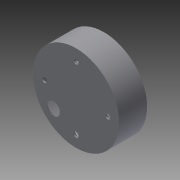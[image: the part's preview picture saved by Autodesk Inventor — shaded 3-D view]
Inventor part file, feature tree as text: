
AUTODESK INVENTOR PART (.ipt)
format: ipt  version: 2014 (Build 180170000, 170)  size: 233,472 bytes
history: native  units: mm
features: sketch x9, extrude x8, chamfer x5, projected_geometry x3, plane x1
ambient origin geometry x8: Origin, YZ Plane, XZ Plane, XY Plane, X Axis, Y Axis, Z Axis, Center Point
bodies: Solid1 (feature_tree)
feature tree (26):
  extrude  "Extrusion1"  Depth=3.0mm TaperAngle=0.0deg
  extrude  "Extrusion2"  Depth=19.0mm TaperAngle=0.0deg
  extrude  "Extrusion3"  Depth=4.0mm
  chamfer  "Chamfer1"  Distance=14.0mm
  extrude  "Extrusion4"  Depth=6.0mm TaperAngle=45.0deg
  chamfer  "Chamfer2"  Distance=10.0mm
  sketch  "Sketch5"  dims[d9=4.0mm]
  extrude  "Extrusion5"  Depth=6.0mm TaperAngle=0.0deg
  extrude  "Extrusion6"  Depth=6.0mm TaperAngle=45.0deg
  chamfer  "Chamfer3"  Distance=25.0mm
  plane  "Work Plane1"
  extrude  "Extrusion9"  Depth=6.0mm
  chamfer  "Chamfer5"  Distance=2.5mm
  extrude  "Extrusion10"  Depth=6.0mm
  chamfer  "Chamfer6"  Distance=6.0mm
  sketch  "Sketch1"  dims[d0=68.0mm d1=3.0mm d2=0.0mm]
  sketch  "Sketch2"  dims[d3=62.0mm d4=19.0mm d5=0.0mm]
  sketch  "Sketch3"  dims[d6=4.0mm d7=4.0mm]
  sketch  "Sketch4"  dims[d8=4.0mm]
  sketch  "Sketch6"  dims[d10=25.0mm]
  sketch  "Sketch7"  dims[d11=25.0mm]
  projected_geometry  "Projected Loop1"
  projected_geometry  "Projected Loop2"
  projected_geometry  "Projected Loop3"
  sketch  "Sketch10"  dims[d12=25.0mm]
  sketch  "Sketch11"  dims[d13=25.0mm d14=14.0mm d15=0.0mm d16=2.0mm d17=2.0mm d18=45.0deg d19=10.0mm d20=14.0mm d21=0.0mm d22=3.0mm d23=2.0mm d24=45.0deg d25=25.0mm d26=40.0mm d27=2.5mm d28=6.0mm d29=2.5mm d30=6.0mm d31=2.5mm d32=6.0mm d33=2.5mm d34=6.0mm d35=25.0mm d36=40.0mm d37=3.0mm d38=3.0mm d39=3.0mm d40=3.0mm d41=3.0mm d42=3.0mm d43=3.0mm d44=3.0mm d45=3.0mm d46=0.0mm d47=2.0mm d48=0.0mm d49=0.6mm d50=2.0mm d51=45.0deg d62=6.0mm d63=0.0mm d64=4.0mm d65=2.0mm d66=45.0deg d67=59.0mm d68=2.0mm d69=2.0mm d70=6.0mm d71=0.0mm d72=0.5mm d73=2.0mm d74=45.0deg]
